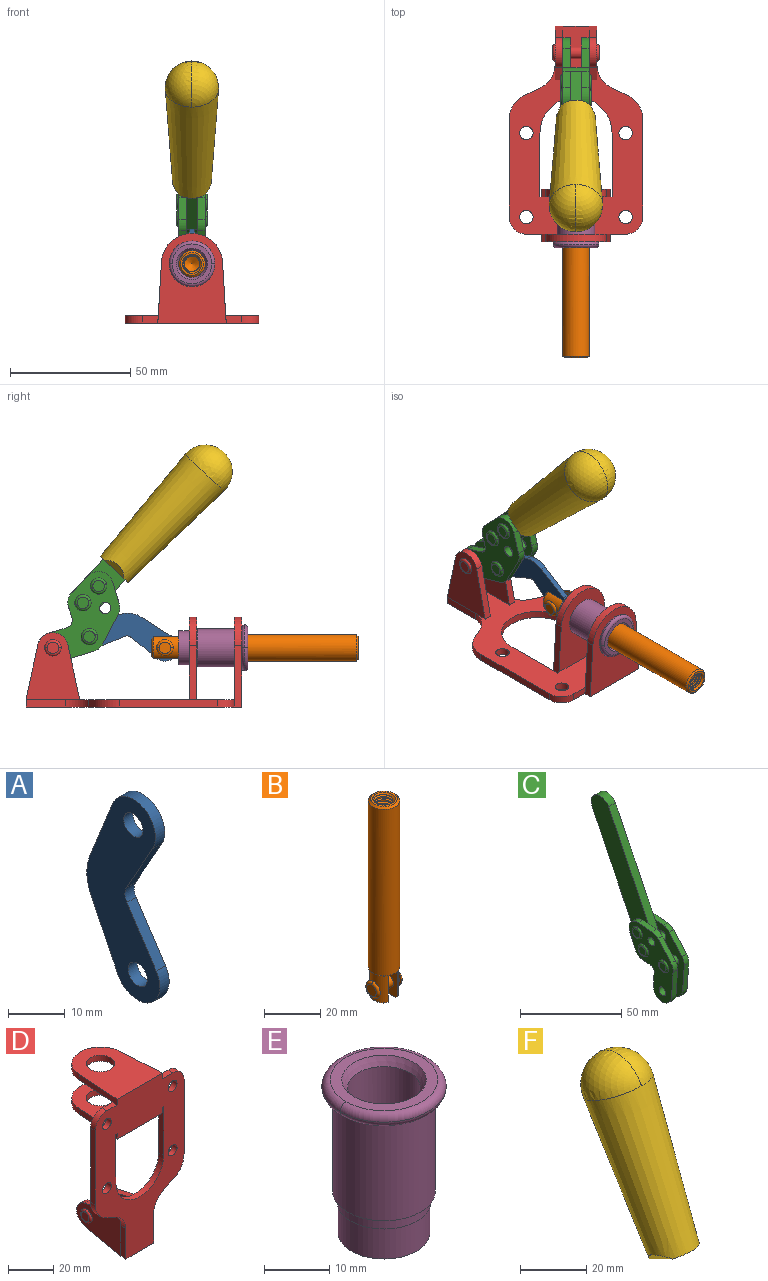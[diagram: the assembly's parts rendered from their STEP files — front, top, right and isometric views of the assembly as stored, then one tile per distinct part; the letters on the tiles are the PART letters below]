
ASSEMBLY  parts=6 mates=6
PART A: 12 faces, bbox 2.3x18.2x42.8 mm
  f0: cylinder r=2.4mm len=4.8mm, axis (1,0,0), area 34.9mm2, adj f4,f11
  f1: cylinder r=10.41mm len=8.47mm, axis (1,0,0), area 20.2mm2, adj f4,f9,f10,f11
  f2: cylinder r=3.05mm len=3.16mm, axis (1,0,0), area 7.7mm2, adj f4,f6,f7,f11
  f3: cylinder r=2.4mm len=4.8mm, axis (1,0,0), area 34.9mm2, adj f4,f11
  f4: plane 42.81x18.23mm, normal (-1,0,0), area 414.1mm2, adj f0,f1,f2,f3,f5,f6,f7,f8
  f5: cylinder r=5.54mm len=10.67mm, axis (1,0,0), area 41.8mm2, adj f4,f6,f10,f11
  f6: plane 11.66x6.53mm, normal (0,-0.87,-0.49), area 30.9mm2, adj f2,f4,f5,f11
  f7: plane 11.17x7.33mm, normal (0,-0.84,0.55), area 30.9mm2, adj f2,f4,f8,f11
  f8: cylinder r=5.54mm len=10.51mm, axis (1,0,0), area 41.8mm2, adj f4,f7,f9,f11
  f9: plane 13.67x6.67mm, normal (0,0.9,-0.44), area 35.1mm2, adj f1,f4,f8,f11
  f10: plane 14.1x5.7mm, normal (0,0.93,0.37), area 35.1mm2, adj f1,f4,f5,f11
  f11: plane 42.81x18.23mm, normal (1,0,0), area 414.1mm2, adj f0,f1,f2,f3,f5,f6,f7,f8
PART B: 48 faces, bbox 12.6x11.1x86.1 mm
  f0: torus R=2.41mm, axis (-1,0,0), area 15mm2, adj f30,f32,f34
  f1: torus R=2.41mm, axis (-1,0,0), area 15mm2, adj f29,f31,f33
  f2: cylinder r=5.54mm len=72.39mm, axis (0,0,1), area 2518.5mm2, adj f3,f4,f42,f43
  f3: cone r=5.54mm half-angle=45deg, axis (0,0,1), area 7.6mm2, adj f2,f5,f41
  f4: cone r=5.54mm half-angle=45deg, axis (0,0,-1), area 34.9mm2, adj f2,f39
  f5: cylinder r=5.08mm len=11.48mm, axis (0,0,1), area 108.3mm2, adj f3,f7,f8,f41
  f6: cylinder r=2.41mm len=4.83mm, axis (-1,0,0), area 71.2mm2, adj f40,f41
  f7: cylinder r=2.41mm len=4.83mm, axis (-1,0,0), area 7.6mm2, adj f5,f34
  f8: cone r=5.08mm half-angle=45deg, axis (0,0,1), area 10.6mm2, adj f5,f37,f41
  f9: cone r=3.98mm half-angle=45deg, axis (0,0,1), area 17.6mm2, adj f27,f39,f45,f46,f47
  f10: cylinder r=2.41mm len=4.83mm, axis (-1,0,0), area 7.6mm2, adj f33,f38
  f11: cylinder r=3.2mm len=6.4mm, axis (0,0,1), area 78.4mm2, adj f12,f28,f44,f45,f47
  f12: cylinder r=3.2mm len=6.4mm, axis (0,0,1), area 10.5mm2, adj f11,f13,f45,f47
  f13: cylinder r=3.2mm len=6.4mm, axis (0,0,1), area 10.5mm2, adj f12,f14,f45,f47
  f14: cylinder r=3.2mm len=6.4mm, axis (0,0,1), area 10.5mm2, adj f13,f15,f45,f47
  f15: cylinder r=3.2mm len=6.4mm, axis (0,0,1), area 10.5mm2, adj f14,f16,f45,f47
  f16: cylinder r=3.2mm len=6.4mm, axis (0,0,1), area 10.5mm2, adj f15,f17,f45,f47
  f17: cylinder r=3.2mm len=6.4mm, axis (0,0,1), area 10.5mm2, adj f16,f18,f45,f47
  f18: cylinder r=3.2mm len=6.4mm, axis (0,0,1), area 10.5mm2, adj f17,f19,f45,f47
  f19: cylinder r=3.2mm len=6.4mm, axis (0,0,1), area 10.5mm2, adj f18,f20,f45,f47
  f20: cylinder r=3.2mm len=6.4mm, axis (0,0,1), area 10.5mm2, adj f19,f21,f45,f47
  f21: cylinder r=3.2mm len=6.4mm, axis (0,0,1), area 10.5mm2, adj f20,f22,f45,f47
  f22: cylinder r=3.2mm len=6.4mm, axis (0,0,1), area 10.5mm2, adj f21,f23,f45,f47
  f23: cylinder r=3.2mm len=6.4mm, axis (0,0,1), area 10.5mm2, adj f22,f24,f45,f47
  f24: cylinder r=3.2mm len=6.4mm, axis (0,0,1), area 10.5mm2, adj f23,f25,f45,f47
  f25: cylinder r=3.2mm len=6.4mm, axis (0,0,1), area 10.5mm2, adj f24,f26,f45,f47
  f26: cylinder r=3.2mm len=6.4mm, axis (0,0,1), area 10.5mm2, adj f25,f27,f45,f47
  f27: cylinder r=3.2mm len=6.4mm, axis (0,0,1), area 7.4mm2, adj f9,f26,f45,f47
  f28: cone r=3.2mm half-angle=60deg, axis (0,0,1), area 37.2mm2, adj f11
  f29: plane 4.83x4.83mm, normal (-1,0,0), area 18.3mm2, adj f1,f31
  f30: plane 4.83x4.83mm, normal (1,0,0), area 18.3mm2, adj f0,f32
  f31: torus R=2.41mm, axis (-1,0,0), area 15mm2, adj f1,f29,f33
  f32: torus R=2.41mm, axis (-1,0,0), area 15mm2, adj f0,f30,f34
  f33: plane 6.83x6.83mm, normal (1,0,0), area 18.3mm2, adj f1,f10,f31
  f34: plane 6.83x6.83mm, normal (-1,0,0), area 18.3mm2, adj f0,f7,f32
  f35: cone r=5.08mm half-angle=45deg, axis (0,0,1), area 10.6mm2, adj f36,f38,f40
  f36: plane 7.25x1.97mm, normal (0,0,-1), area 10mm2, adj f35,f40
  f37: plane 7.25x1.97mm, normal (0,0,-1), area 10mm2, adj f8,f41
  f38: cylinder r=5.08mm len=11.48mm, axis (0,0,1), area 108.3mm2, adj f10,f35,f40,f42
  f39: plane 9.55x9.55mm, normal (0,0,1), area 22mm2, adj f4,f9
  f40: plane 12.76x10.09mm, normal (1,0,0), area 95.7mm2, adj f6,f35,f36,f38,f42,f43
  f41: plane 12.76x10.09mm, normal (-1,0,0), area 95.7mm2, adj f3,f5,f6,f8,f37,f43
  f42: cone r=5.54mm half-angle=45deg, axis (0,0,1), area 7.6mm2, adj f2,f38,f40
  f43: plane 11.07x4.7mm, normal (0,0,-1), area 50.4mm2, adj f2,f40,f41
  f44: plane 0.89x0.62mm, normal (-1,0,0), area 0.3mm2, adj f11,f45,f46,f47
  f45: bspline ~24.8x7.63mm, area 266.6mm2, adj f9,f11,f12,f13,f14,f15,f16,f17
  f46: bspline ~24.87x7.63mm, area 73.6mm2, adj f9,f44,f45,f47
  f47: bspline ~24.98x7.63mm, area 272.5mm2, adj f9,f11,f12,f13,f14,f15,f16,f17
PART C: 59 faces, bbox 12.9x60.2x99.6 mm
  f0: torus R=2.39mm, axis (-1,0,0), area 14.9mm2, adj f20,f43,f51
  f1: torus R=2.39mm, axis (-1,0,0), area 14.9mm2, adj f19,f42,f51
  f2: torus R=2.39mm, axis (-1,0,0), area 14.9mm2, adj f18,f35,f51
  f3: torus R=2.39mm, axis (-1,0,0), area 14.9mm2, adj f14,f17,f23
  f4: torus R=2.39mm, axis (-1,0,0), area 14.9mm2, adj f13,f16,f23
  f5: torus R=2.39mm, axis (-1,0,0), area 14.9mm2, adj f12,f15,f23
  f6: cylinder r=2.39mm len=4.78mm, axis (1,0,0), area 46.5mm2, adj f48,f50,f51
  f7: cylinder r=2.39mm len=4.78mm, axis (1,0,0), area 46.5mm2, adj f50,f51
  f8: cylinder r=6.35mm len=12.68mm, axis (1,0,0), area 61.8mm2, adj f38,f39,f50,f51
  f9: cylinder r=2.39mm len=4.78mm, axis (-1,0,0), area 70.5mm2, adj f46,f50
  f10: cylinder r=2.39mm len=4.78mm, axis (-1,0,0), area 46.5mm2, adj f23,f45,f46
  f11: cylinder r=2.39mm len=4.78mm, axis (-1,0,0), area 46.5mm2, adj f23,f46
  f12: plane 4.78x4.78mm, normal (1,0,0), area 17.9mm2, adj f5,f15
  f13: plane 4.78x4.78mm, normal (1,0,0), area 17.9mm2, adj f4,f16
  f14: plane 4.78x4.78mm, normal (1,0,0), area 17.9mm2, adj f3,f17
  f15: torus R=2.39mm, axis (-1,0,0), area 14.9mm2, adj f5,f12,f23
  f16: torus R=2.39mm, axis (-1,0,0), area 14.9mm2, adj f4,f13,f23
  f17: torus R=2.39mm, axis (-1,0,0), area 14.9mm2, adj f3,f14,f23
  f18: plane 4.78x4.78mm, normal (-1,0,0), area 17.9mm2, adj f2,f35
  f19: plane 4.78x4.78mm, normal (-1,0,0), area 17.9mm2, adj f1,f42
  f20: plane 4.78x4.78mm, normal (-1,0,0), area 17.9mm2, adj f0,f43
  f21: plane 2.26x0.2mm, normal (1,0,0), area 0.2mm2, adj f31,f44
  f22: plane 2.26x0.2mm, normal (-1,0,0), area 0.2mm2, adj f41,f44
  f23: plane 39.37x30.77mm, normal (1,0,0), area 565.5mm2, adj f3,f4,f5,f10,f11,f15,f16,f17
  f24: cylinder r=6.1mm len=4.15mm, axis (-1,0,0), area 14.7mm2, adj f23,f25,f32,f46
  f25: plane 10.25x9.01mm, normal (0,-0.75,0.66), area 42.3mm2, adj f23,f24,f26,f46
  f26: cylinder r=6.35mm len=4.64mm, axis (-1,0,0), area 15.6mm2, adj f23,f25,f27,f46
  f27: plane 15.84x3.1mm, normal (0,-1,-0.07), area 49.2mm2, adj f23,f26,f28,f46
  f28: cylinder r=6.35mm len=12.68mm, axis (-1,0,0), area 61.8mm2, adj f23,f27,f29,f46
  f29: plane 8.11x3.1mm, normal (0,1,0.07), area 25.2mm2, adj f23,f28,f30,f46
  f30: cylinder r=3.05mm len=3.25mm, axis (-1,0,0), area 14.8mm2, adj f23,f29,f31,f46
  f31: plane 5.99x3.1mm, normal (0,0.07,-1), area 18.6mm2, adj f21,f23,f30,f44,f46
  f32: plane 9.5x3.1mm, normal (0,-0.07,1), area 29.5mm2, adj f23,f24,f33,f46,f47
  f33: cylinder r=6.1mm len=8.63mm, axis (-1,0,0), area 39.1mm2, adj f23,f32,f34,f47
  f34: plane 8.65x3.96mm, normal (0,0.91,-0.42), area 29.5mm2, adj f23,f33,f44,f47
  f35: torus R=2.39mm, axis (-1,0,0), area 14.9mm2, adj f2,f18,f51
  f36: plane 10.25x9.01mm, normal (0,-0.75,0.66), area 42.3mm2, adj f37,f49,f50,f51
  f37: cylinder r=6.35mm len=4.64mm, axis (1,0,0), area 15.6mm2, adj f36,f38,f50,f51
  f38: plane 15.84x3.1mm, normal (0,-1,-0.07), area 49.2mm2, adj f8,f37,f50,f51
  f39: plane 8.11x3.1mm, normal (0,1,0.07), area 25.2mm2, adj f8,f40,f50,f51
  f40: cylinder r=3.05mm len=3.25mm, axis (1,0,0), area 14.8mm2, adj f39,f41,f50,f51
  f41: plane 5.99x3.1mm, normal (0,0.07,-1), area 18.6mm2, adj f22,f40,f44,f50,f51
  f42: torus R=2.39mm, axis (-1,0,0), area 14.9mm2, adj f1,f19,f51
  f43: torus R=2.39mm, axis (-1,0,0), area 14.9mm2, adj f0,f20,f51
  f44: cylinder r=6.35mm len=12.12mm, axis (-1,0,0), area 128.9mm2, adj f21,f22,f23,f31,f34,f41,f46,f47
  f45: plane 2.65x1.35mm, normal (1,0,0), area 1mm2, adj f10,f55
  f46: plane 39.08x20.42mm, normal (-1,0,0), area 412.5mm2, adj f9,f10,f11,f24,f25,f26,f27,f28
  f47: plane 77.62x39.82mm, normal (1,0,0), area 850mm2, adj f32,f33,f34,f44,f53,f54,f55
  f48: plane 2.65x1.35mm, normal (-1,0,0), area 1mm2, adj f6,f55
  f49: cylinder r=6.1mm len=4.15mm, axis (1,0,0), area 14.7mm2, adj f36,f50,f51,f56
  f50: plane 39.08x20.42mm, normal (1,0,0), area 412.5mm2, adj f6,f7,f8,f9,f36,f37,f38,f39
  f51: plane 39.37x30.77mm, normal (-1,0,0), area 565.5mm2, adj f0,f1,f2,f6,f7,f8,f35,f36
  f52: plane 8.65x3.96mm, normal (0,0.91,-0.42), area 29.5mm2, adj f44,f51,f57,f58
  f53: plane 68.49x33.4mm, normal (0,0.9,-0.44), area 358.1mm2, adj f44,f47,f54,f58
  f54: cylinder r=6.35mm len=12.06mm, axis (1,0,0), area 93.7mm2, adj f47,f53,f55,f58
  f55: plane 68.49x33.4mm, normal (0,-0.9,0.44), area 358.1mm2, adj f44,f45,f46,f47,f48,f50,f54,f58
  f56: plane 9.5x3.1mm, normal (0,-0.07,1), area 29.5mm2, adj f49,f50,f51,f57,f58
  f57: cylinder r=6.1mm len=8.63mm, axis (1,0,0), area 39.1mm2, adj f51,f52,f56,f58
  f58: plane 77.62x39.82mm, normal (-1,0,0), area 850mm2, adj f44,f52,f53,f54,f55,f56,f57
PART D: 55 faces, bbox 55.7x37.4x89.8 mm
  f0: torus R=2.41mm, axis (-1,0,0), area 15mm2, adj f11,f15,f25
  f1: torus R=2.41mm, axis (-1,0,0), area 15mm2, adj f10,f12,f22
  f2: cylinder r=2.78mm len=5.56mm, axis (0,-1,0), area 54.2mm2, adj f30,f54
  f3: cylinder r=14.99mm len=29.97mm, axis (0,-1,0), area 145.9mm2, adj f30,f49,f53,f54
  f4: cylinder r=2.78mm len=5.56mm, axis (0,-1,0), area 54.2mm2, adj f30,f54
  f5: cylinder r=2.78mm len=5.56mm, axis (0,-1,0), area 54.2mm2, adj f30,f54
  f6: cylinder r=2.78mm len=5.56mm, axis (0,-1,0), area 54.2mm2, adj f30,f54
  f7: cylinder r=6.35mm len=12.7mm, axis (0,0,1), area 123.6mm2, adj f27,f51
  f8: cylinder r=6.35mm len=12.7mm, axis (0,0,-1), area 124.7mm2, adj f21,f35
  f9: cylinder r=2.41mm len=11.18mm, axis (-1,0,0), area 169.4mm2, adj f16,f19
  f10: plane 4.83x4.83mm, normal (1,0,0), area 18.3mm2, adj f1,f12
  f11: plane 4.83x4.83mm, normal (-1,0,0), area 18.3mm2, adj f0,f15
  f12: torus R=2.41mm, axis (-1,0,0), area 15mm2, adj f1,f10,f22
  f13: cylinder r=6.35mm len=12.41mm, axis (1,0,0), area 53.4mm2, adj f18,f19,f22,f23
  f14: cylinder r=6.35mm len=12.41mm, axis (-1,0,0), area 53.4mm2, adj f16,f17,f24,f25
  f15: torus R=2.41mm, axis (-1,0,0), area 15mm2, adj f0,f11,f25
  f16: plane 27.86x22.35mm, normal (1,0,0), area 425.4mm2, adj f9,f14,f17,f24,f30
  f17: plane 22.86x4.97mm, normal (0,0.21,0.98), area 72.5mm2, adj f14,f16,f25,f30
  f18: plane 22.86x4.97mm, normal (0,0.21,0.98), area 72.5mm2, adj f13,f19,f22,f30
  f19: plane 27.86x22.35mm, normal (-1,0,0), area 425.4mm2, adj f9,f13,f18,f23,f30
  f20: cylinder r=12.7mm len=25.35mm, axis (0,0,-1), area 119.8mm2, adj f21,f34,f35,f36
  f21: plane 34.21x28.07mm, normal (0,0,-1), area 702.4mm2, adj f8,f20,f30,f34,f36
  f22: plane 27.96x22.45mm, normal (1,0,0), area 407.2mm2, adj f1,f12,f13,f18,f23,f30,f42,f43
  f23: plane 22.86x4.97mm, normal (0,0.21,-0.98), area 72.5mm2, adj f13,f19,f22,f44
  f24: plane 22.86x4.97mm, normal (0,0.21,-0.98), area 72.5mm2, adj f14,f16,f25,f44
  f25: plane 27.86x22.35mm, normal (-1,0,0), area 407.1mm2, adj f0,f14,f15,f17,f24,f30,f45,f46
  f26: plane 3.1x0.95mm, normal (0,0,-1), area 2.7mm2, adj f30,f49,f50,f54
  f27: plane 34.21x28.07mm, normal (0,0,1), area 702.4mm2, adj f7,f28,f30,f50,f52
  f28: cylinder r=12.7mm len=25.35mm, axis (0,0,1), area 118.8mm2, adj f27,f50,f51,f52
  f29: plane 3.1x0.95mm, normal (0,0,-1), area 2.7mm2, adj f30,f52,f53,f54
  f30: plane 86.54x55.63mm, normal (0,1,0), area 2362.9mm2, adj f2,f3,f4,f5,f6,f16,f17,f18
  f31: plane 40.56x3.1mm, normal (-1,0,0), area 125.7mm2, adj f30,f32,f48,f54
  f32: cylinder r=7.11mm len=7.11mm, axis (0,-1,0), area 34.6mm2, adj f30,f31,f33,f54
  f33: plane 6.67x3.1mm, normal (0,0,1), area 20.4mm2, adj f30,f32,f34,f54
  f34: plane 25.39x3.13mm, normal (-1,0.06,0), area 79.5mm2, adj f20,f21,f33,f35,f54
  f35: plane 37.31x28.45mm, normal (0,0,1), area 789.9mm2, adj f8,f20,f34,f36,f54
  f36: plane 25.39x3.13mm, normal (1,0.06,0), area 79.5mm2, adj f20,f21,f35,f37,f54
  f37: plane 6.67x3.1mm, normal (0,0,1), area 20.4mm2, adj f30,f36,f38,f54
  f38: cylinder r=7.11mm len=7.11mm, axis (0,-1,0), area 34.6mm2, adj f30,f37,f39,f54
  f39: plane 40.56x3.1mm, normal (1,0,0), area 125.7mm2, adj f30,f38,f40,f54
  f40: cylinder r=11.18mm len=10.16mm, axis (0,-1,0), area 39.5mm2, adj f30,f39,f41,f54
  f41: plane 6.09x3.1mm, normal (0.42,0,-0.91), area 20.8mm2, adj f30,f40,f42,f54
  f42: cylinder r=11.18mm len=9.41mm, axis (0,-1,0), area 37.2mm2, adj f22,f30,f41,f43,f54
  f43: plane 16.5x3.1mm, normal (1,0,0), area 51.1mm2, adj f22,f42,f44,f54
  f44: plane 17.37x3.1mm, normal (0,0,-1), area 53.8mm2, adj f23,f24,f30,f43,f45,f54
  f45: plane 16.5x3.1mm, normal (-1,0,0), area 51.1mm2, adj f25,f44,f46,f54
  f46: cylinder r=11.18mm len=9.41mm, axis (0,-1,0), area 37.2mm2, adj f25,f30,f45,f47,f54
  f47: plane 6.09x3.1mm, normal (-0.42,0,-0.91), area 20.8mm2, adj f30,f46,f48,f54
  f48: cylinder r=11.18mm len=10.16mm, axis (0,-1,0), area 39.5mm2, adj f30,f31,f47,f54
  f49: plane 26.54x3.1mm, normal (-1,0,0), area 82.3mm2, adj f3,f26,f30,f54
  f50: plane 25.39x3.1mm, normal (1,0.06,0), area 78.8mm2, adj f26,f27,f28,f51,f54
  f51: plane 37.31x28.45mm, normal (0,0,-1), area 789.9mm2, adj f7,f28,f50,f52,f54
  f52: plane 25.39x3.1mm, normal (-1,0.06,0), area 78.8mm2, adj f27,f28,f29,f51,f54
  f53: plane 26.54x3.1mm, normal (1,0,0), area 82.3mm2, adj f3,f29,f30,f54
  f54: plane 89.66x55.63mm, normal (0,-1,0), area 2678.5mm2, adj f2,f3,f4,f5,f6,f26,f29,f31
PART E: 15 faces, bbox 20.6x20.6x28.7 mm
  f0: torus R=8.26mm, axis (0,0,1), area 56.8mm2, adj f1,f10,f12
  f1: torus R=8.26mm, axis (0,0,1), area 56.8mm2, adj f0,f6,f13
  f2: cylinder r=5.59mm len=25.91mm, axis (0,0,1), area 909.6mm2, adj f3,f4
  f3: cone r=6.86mm half-angle=45deg, axis (0,0,-1), area 70.2mm2, adj f2,f14
  f4: cone r=6.47mm half-angle=30deg, axis (0,0,1), area 66.7mm2, adj f2,f13
  f5: cylinder r=7.04mm len=14.07mm, axis (0,0,1), area 252.6mm2, adj f11,f14
  f6: torus R=8.26mm, axis (0,0,1), area 56.8mm2, adj f1,f12,f13
  f7: cylinder r=7.16mm len=14.33mm, axis (0,0,1), area 91.5mm2, adj f9,f11
  f8: cylinder r=7.86mm len=18.42mm, axis (0,0,1), area 909.6mm2, adj f9,f10
  f9: plane 15.72x15.72mm, normal (0,0,-1), area 33mm2, adj f7,f8
  f10: plane 16.51x16.51mm, normal (0,0,-1), area 19.9mm2, adj f0,f8,f12
  f11: plane 14.33x14.33mm, normal (0,0,-1), area 5.7mm2, adj f5,f7
  f12: torus R=8.26mm, axis (0,0,1), area 56.8mm2, adj f0,f6,f10
  f13: plane 16.51x16.51mm, normal (0,0,1), area 82.7mm2, adj f1,f4,f6
  f14: plane 14.07x14.07mm, normal (0,0,-1), area 7.8mm2, adj f3,f5
PART F: 11 faces, bbox 22.3x42.6x64.5 mm
  f0: sphere r=11.13mm, area 411.4mm2, adj f1,f8
  f1: cone r=11.11mm half-angle=3.3deg, axis (0,0.44,0.9), area 3251.8mm2, adj f0,f7,f8,f9,f10
  f2: cylinder r=6.16mm len=11.7mm, axis (1,0,0), area 89.5mm2, adj f3,f4,f5,f6
  f3: plane 60.23x36.75mm, normal (-1,0,0), area 763.6mm2, adj f2,f4,f6,f10
  f4: plane 51.37x25.05mm, normal (0,0.9,-0.44), area 264.2mm2, adj f2,f3,f5,f10
  f5: plane 60.23x36.75mm, normal (1,0,0), area 763.6mm2, adj f2,f4,f6,f10
  f6: plane 51.37x25.05mm, normal (0,-0.9,0.44), area 264.2mm2, adj f2,f3,f5,f10
  f7: plane 9.95x5.95mm, normal (0.71,-0.31,-0.64), area 25.8mm2, adj f1,f10
  f8: sphere r=11.13mm, area 411.4mm2, adj f0,f1
  f9: plane 9.95x5.95mm, normal (-0.71,-0.31,-0.64), area 25.8mm2, adj f1,f10
  f10: plane 14.27x11.38mm, normal (0,-0.44,-0.9), area 106.7mm2, adj f1,f3,f4,f5,f6,f7,f9
PLACE A rot(axis=(0,-0.67,-0.75),180deg) t=(0,13.69,3.06)mm
PLACE B rot(axis=(1,0,0),90deg) t=(0,10.4,0)mm
PLACE C rot(axis=(1,0,0),69.1deg) t=(0,2.76,13.09)mm
PLACE D rot(axis=(1,0,0),90deg) t=(0,9.43,0)mm fixed
PLACE E rot(axis=(1,0,0),90deg) t=(0,9.43,0)mm
PLACE F rot(axis=(1,0,0),69.1deg) t=(-0.04,2.76,13.09)mm
MATE fastened F.f2 <-> C.f54  axis (1,0,0) through (-2.35,-23.03,99.01)mm
MATE slider B.f2 <-> D.f7  axis (0,-1,0) through (0,-48.38,24.61)mm
MATE revolute A.f3 <-> B.f6  axis (-1,0,0) through (0,-5.08,24.61)mm
MATE revolute A.f5 <-> C.f4  axis (-1,0,0) through (0,26.34,29.23)mm
MATE revolute C.f7 <-> D.f0  axis (-1,0,0) through (0,41.52,24.61)mm
MATE fastened E.f2 <-> D.f7  axis (0,1,0) through (0,-36.96,24.61)mm
